# Revit family: MBS_closet with door
name_source: partatom
category: Generic Models
revit_build: Autodesk Revit 2014 (Build: 20130308_1515(x64)
units: mm (PartAtom-declared; Revit-internal decimal feet)

## types (5) — shared parameters
panel thickness = 30 mm  [stored 0.0984252 ft]

## per-type parameters (varying)
| type | c_close door widht | c_closet back height | c_closet back widht | c_closet base depht | c_closet base widht | c_closet door height | c_closet side height | c_closet side widht | c_closet top depht | c_closet top widht | c_shelf depht | c_shelf widht | closet with door material |
| bathroom closet | 350 mm  [stored 1.14829 ft] | 1500 mm  [stored 4.92126 ft] | 700 mm  [stored 2.29659 ft] | 490 mm  [stored 1.60761 ft] | 640 mm  [stored 2.09974 ft] | 1470 mm | 1500 mm  [stored 4.92126 ft] | 490 mm  [stored 1.60761 ft] | 490 mm  [stored 1.60761 ft] | 640 mm  [stored 2.09974 ft] | 490 mm  [stored 1.60761 ft] | 640 mm  [stored 2.09974 ft] | Oak, White CLOSET WITH DOOR MBS |
| kitchen closet | 300 mm | 820 mm  [stored 2.69029 ft] | 600 mm | 540 mm  [stored 1.77165 ft] | 540 mm  [stored 1.77165 ft] | 790 mm  [stored 2.59186 ft] | 820 mm  [stored 2.69029 ft] | 540 mm  [stored 1.77165 ft] | 540 mm  [stored 1.77165 ft] | 540 mm  [stored 1.77165 ft] | 540 mm  [stored 1.77165 ft] | 540 mm  [stored 1.77165 ft] | Walnut KITCHEN CLOSET MBS |
| wardrobe main bedroom | 300 mm | 1500 mm  [stored 4.92126 ft] | 600 mm | 540 mm  [stored 1.77165 ft] | 540 mm  [stored 1.77165 ft] | 1470 mm | 1500 mm  [stored 4.92126 ft] | 540 mm  [stored 1.77165 ft] | 540 mm  [stored 1.77165 ft] | 540 mm  [stored 1.77165 ft] | 540 mm  [stored 1.77165 ft] | 540 mm  [stored 1.77165 ft] | Laminate, Ivory, Matte WARDROBE MBS |
| fridge | 300 mm | 1800 mm  [stored 5.90551 ft] | 600 mm | 580 mm  [stored 1.90289 ft] | 540 mm  [stored 1.77165 ft] | 1770 mm | 1800 mm  [stored 5.90551 ft] | 580 mm  [stored 1.90289 ft] | 580 mm  [stored 1.90289 ft] | 540 mm  [stored 1.77165 ft] | 580 mm  [stored 1.90289 ft] | 540 mm  [stored 1.77165 ft] | Walnut KITCHEN CLOSET MBS |
| wardrobe second bedroom | 300 mm | 1500 mm  [stored 4.92126 ft] | 600 mm | 540 mm  [stored 1.77165 ft] | 540 mm  [stored 1.77165 ft] | 1470 mm | 1500 mm  [stored 4.92126 ft] | 540 mm  [stored 1.77165 ft] | 540 mm  [stored 1.77165 ft] | 540 mm  [stored 1.77165 ft] | 540 mm  [stored 1.77165 ft] | 540 mm  [stored 1.77165 ft] | Polyvinyl Chloride, Rigid WARDROBE2 MBS |

note: [stored X ft] marks values corroborated as IEEE doubles in the binary element streams (Revit-internal decimal feet)

## geometry (parser evidence)
native form markers: Sweep x1
no freeform markers — native parametric forms only
